# Revit family: mcr FID C
name_source: partatom
category: Akcesoria wentylacyjne
revit_build: Autodesk Revit 2015 (Build: 20160512_1515(x64)
units: mm (PartAtom-declared; Revit-internal decimal feet)

## types (36) — shared parameters
Dokumentacja techniczna = https://mercor.com.pl
Długość = 296 mm  [stored 0.971129 ft]
IfcExportAs = IfcDamperType
IfcExportType = FIREDAMPER
Klasyfikacja obciążenia = Inne
Model = mcr FID S/S c/P
Opis = Niskooporowa przeciwpożarowa klapa jednopłaszczyznowa odcinająca do systemów wentylacji bytowej
Producent = Mercor
URL = http://www.mercor.com.pl

## per-type parameters (varying)
| type | A | E | F | Materiał klapy | Moc pozorna | Napięcie | Nazwa sterowania | Numer | Opis sterowania |
| mcr FID S/S c/P, RST, stal ocynkowana | 50 mm  [stored 0.164042 ft] | 70 mm  [stored 0.229659 ft] | 90 mm  [stored 0.295276 ft] | Mercor - stal ocynkowana, powłoka Zn 275 g/m2 | 0 VA | 0 V | RST | 1 | wyzwalacz termiczny |
| mcr FID S/S c/P, RST/WK1, stal ocynkowana | 50 mm  [stored 0.164042 ft] | 70 mm  [stored 0.229659 ft] | 90 mm  [stored 0.295276 ft] | Mercor - stal ocynkowana, powłoka Zn 275 g/m2 | 0 VA | 0 V | RST/WK1 | 1 | wyzwalacz termiczny + wyłącznik krańcowy (sygnalizacja przegrody zamkniętej) |
| mcr FID S/S c/P, RST/WK2, stal ocynkowana | 50 mm  [stored 0.164042 ft] | 70 mm  [stored 0.229659 ft] | 90 mm  [stored 0.295276 ft] | Mercor - stal ocynkowana, powłoka Zn 275 g/m2 | 0 VA | 0 V | RST/WK2 | 1 | wyzwalacz termiczny + wyłącznik krańcowy (sygnalizacja przegrody zamkniętej/otwartej) |
| mcr FID S/S c/P, RST-KW1/S, stal ocynkowana | 130 mm  [stored 0.426509 ft] | 80 mm  [stored 0.262467 ft] | 100 mm  [stored 0.328084 ft] | Mercor - stal ocynkowana, powłoka Zn 275 g/m2 | 0 VA | 0 V | RST-KW1/S | 2 | wyzwalacz termiczny |
| mcr FID S/S c/P, RST-KW1/S/WK2, stal ocynkowana | 130 mm  [stored 0.426509 ft] | 80 mm  [stored 0.262467 ft] | 100 mm  [stored 0.328084 ft] | Mercor - stal ocynkowana, powłoka Zn 275 g/m2 | 0 VA | 0 V | RST-KW1/S/WK2 | 2 | wyzwalacz termiczny + wyłącznik krańcowy (sygnalizacja przegrody zamkniętej/otwartej) |
| mcr FID S/S c/P, RST-KW1/24I, stal ocynkowana | 130 mm  [stored 0.426509 ft] | 80 mm  [stored 0.262467 ft] | 100 mm  [stored 0.328084 ft] | Mercor - stal ocynkowana, powłoka Zn 275 g/m2 | 4 VA | 24 V | RST-KW1/24I | 2 | wyzwalacz termiczny + wyzwalacz elektromagnetyczny typu impuls, U = 24 V DC + wyłącznik krańcowy (sygnalizacja przegrody zamkniętej/otwartej) |
| mcr FID S/S c/P, RST-KW1/24P, stal ocynkowana | 130 mm  [stored 0.426509 ft] | 80 mm  [stored 0.262467 ft] | 100 mm  [stored 0.328084 ft] | Mercor - stal ocynkowana, powłoka Zn 275 g/m2 | 2 VA | 24 V | RST-KW1/24P | 2 | wyzwalacz termiczny + wyzwalacz elektromagnetyczny typu przerwa, U = 24 V DC + wyłącznik krańcowy (sygnalizacja przegrody zamkniętej/otwartej) |
| mcr FID S/S c/P, RST-KW1/230I, stal ocynkowana | 130 mm  [stored 0.426509 ft] | 80 mm  [stored 0.262467 ft] | 100 mm  [stored 0.328084 ft] | Mercor - stal ocynkowana, powłoka Zn 275 g/m2 | 5 VA | 230 V | RST-KW1/230I | 2 | wyzwalacz termiczny + wyzwalacz elektromagnetyczny typu impuls, U = 230 V AC + wyłącznik krańcowy (sygnalizacja przegrody zamkniętej/otwartej) |
| mcr FID S/S c/P, RST-KW1/230P, stal ocynkowana | 130 mm  [stored 0.426509 ft] | 80 mm  [stored 0.262467 ft] | 100 mm  [stored 0.328084 ft] | Mercor - stal ocynkowana, powłoka Zn 275 g/m2 | 3 VA | 230 V | RST-KW1/230P | 2 | wyzwalacz termiczny + wyzwalacz elektromagnetyczny typu przerwa, U = 230 V AC + wyłącznik krańcowy (sygnalizacja przegrody zamkniętej/otwartej) |
| mcr FID S/S c/P, BF24TL-T-ST, stal ocynkowana | 198 mm  [stored 0.649606 ft] | 65 mm  [stored 0.213255 ft] | 98 mm  [stored 0.321522 ft] | Mercor - stal ocynkowana, powłoka Zn 275 g/m2 | 10 VA | 24 V | BF24TL-T-ST | 3 | siłownik ze sprężyną powrotną, U = 24 V, sterowanie cyfrowe MP Bus (z opcją BKN230-24MP) |
| mcr FID S/S c/P, EXBF24-T, stal ocynkowana | 225 mm  [stored 0.738189 ft] | 175 mm  [stored 0.574147 ft] | 98 mm  [stored 0.321522 ft] | Mercor - stal ocynkowana, powłoka Zn 275 g/m2 | 10 VA | 24 V | EXBF24-T | 4 | przeciwwybuchowy siłownik ze sprężyną powrotną w wersji Ex, U = 24 V AC/DC |
| mcr FID S/S c/P, EXBF230-T, stal ocynkowana | 225 mm  [stored 0.738189 ft] | 175 mm  [stored 0.574147 ft] | 98 mm  [stored 0.321522 ft] | Mercor - stal ocynkowana, powłoka Zn 275 g/m2 | 13 VA | 230 V | EXBF230-T | 4 | przeciwwybuchowy siłownik ze sprężyną powrotną w wersji Ex, U = 230 V AC |
| mcr FID S/S c/P, BFL24-T, stal ocynkowana | 138 mm  [stored 0.452756 ft] | 53 mm  [stored 0.173885 ft] | 98 mm  [stored 0.321522 ft] | Mercor - stal ocynkowana, powłoka Zn 275 g/m2 | 4 VA | 24 V | BFL24-T | 5 | siłownik ze sprężyną powrotną, U = 24 V AC/DC |
| mcr FID S/S c/P, BFL230-T, stal ocynkowana | 138 mm  [stored 0.452756 ft] | 53 mm  [stored 0.173885 ft] | 98 mm  [stored 0.321522 ft] | Mercor - stal ocynkowana, powłoka Zn 275 g/m2 | 7 VA | 230 V | BFL230-T | 5 | siłownik ze sprężyną powrotną, U = 230 V AC |
| mcr FID S/S c/P, BFL24-T-ST, stal ocynkowana | 138 mm  [stored 0.452756 ft] | 53 mm  [stored 0.173885 ft] | 98 mm  [stored 0.321522 ft] | Mercor - stal ocynkowana, powłoka Zn 275 g/m2 | 4 VA | 24 V | BFL24-T-ST | 5 | siłownik ze sprężyną powrotną, do systemu SBS Control (z opcją BKN230-24) |
| mcr FID S/S c/P, BFN24-T, stal ocynkowana | 157 mm  [stored 0.515092 ft] | 57 mm  [stored 0.187008 ft] | 98 mm  [stored 0.321522 ft] | Mercor - stal ocynkowana, powłoka Zn 275 g/m2 | 6 VA | 24 V | BFN24-T | 6 | siłownik ze sprężyną powrotną, U = 24 V AC/DC |
| mcr FID S/S c/P, BFN230-T, stal ocynkowana | 157 mm  [stored 0.515092 ft] | 57 mm  [stored 0.187008 ft] | 98 mm  [stored 0.321522 ft] | Mercor - stal ocynkowana, powłoka Zn 275 g/m2 | 10 VA | 230 V | BFN230-T | 6 | siłownik ze sprężyną powrotną, U = 230 V AC |
| mcr FID S/S c/P, BFN24-T-ST, stal ocynkowana | 157 mm  [stored 0.515092 ft] | 57 mm  [stored 0.187008 ft] | 98 mm  [stored 0.321522 ft] | Mercor - stal ocynkowana, powłoka Zn 275 g/m2 | 6 VA | 24 V | BFN24-T-ST | 6 | siłownik ze sprężyną powrotną, do systemu SBS Control (z opcją BKN230-24) |
| mcr FID S/S c/P, RST, stal nierdzewna | 50 mm  [stored 0.164042 ft] | 70 mm  [stored 0.229659 ft] | 90 mm  [stored 0.295276 ft] | Mercor - stal nierdzewna, kwasoodporna 1.4404 | 0 VA | 0 V | RST | 1 | wyzwalacz termiczny |
| mcr FID S/S c/P, RST/WK1, stal nierdzewna | 50 mm  [stored 0.164042 ft] | 70 mm  [stored 0.229659 ft] | 90 mm  [stored 0.295276 ft] | Mercor - stal nierdzewna, kwasoodporna 1.4404 | 0 VA | 0 V | RST/WK1 | 1 | wyzwalacz termiczny + wyłącznik krańcowy (sygnalizacja przegrody zamkniętej) |
| mcr FID S/S c/P, RST/WK2, stal nierdzewna | 50 mm  [stored 0.164042 ft] | 70 mm  [stored 0.229659 ft] | 90 mm  [stored 0.295276 ft] | Mercor - stal nierdzewna, kwasoodporna 1.4404 | 0 VA | 0 V | RST/WK2 | 1 | wyzwalacz termiczny + wyłącznik krańcowy (sygnalizacja przegrody zamkniętej/otwartej) |
| mcr FID S/S c/P, RST-KW1/S, stal nierdzewna | 130 mm  [stored 0.426509 ft] | 80 mm  [stored 0.262467 ft] | 100 mm  [stored 0.328084 ft] | Mercor - stal nierdzewna, kwasoodporna 1.4404 | 0 VA | 0 V | RST-KW1/S | 2 | wyzwalacz termiczny |
| mcr FID S/S c/P, RST-KW1/S/WK2, stal nierdzewna | 130 mm  [stored 0.426509 ft] | 80 mm  [stored 0.262467 ft] | 100 mm  [stored 0.328084 ft] | Mercor - stal nierdzewna, kwasoodporna 1.4404 | 0 VA | 0 V | RST-KW1/S/WK2 | 2 | wyzwalacz termiczny + wyłącznik krańcowy (sygnalizacja przegrody zamkniętej/otwartej) |
| mcr FID S/S c/P, RST-KW1/24I, stal nierdzewna | 130 mm  [stored 0.426509 ft] | 80 mm  [stored 0.262467 ft] | 100 mm  [stored 0.328084 ft] | Mercor - stal nierdzewna, kwasoodporna 1.4404 | 4 VA | 24 V | RST-KW1/24I | 2 | wyzwalacz termiczny + wyzwalacz elektromagnetyczny typu impuls, U = 24 V DC + wyłącznik krańcowy (sygnalizacja przegrody zamkniętej/otwartej) |
| mcr FID S/S c/P, RST-KW1/24P, stal nierdzewna | 130 mm  [stored 0.426509 ft] | 80 mm  [stored 0.262467 ft] | 100 mm  [stored 0.328084 ft] | Mercor - stal nierdzewna, kwasoodporna 1.4404 | 2 VA | 24 V | RST-KW1/24P | 2 | wyzwalacz termiczny + wyzwalacz elektromagnetyczny typu przerwa, U = 24 V DC + wyłącznik krańcowy (sygnalizacja przegrody zamkniętej/otwartej) |
| mcr FID S/S c/P, RST-KW1/230I, stal nierdzewna | 130 mm  [stored 0.426509 ft] | 80 mm  [stored 0.262467 ft] | 100 mm  [stored 0.328084 ft] | Mercor - stal nierdzewna, kwasoodporna 1.4404 | 5 VA | 230 V | RST-KW1/230I | 2 | wyzwalacz termiczny + wyzwalacz elektromagnetyczny typu impuls, U = 230 V AC + wyłącznik krańcowy (sygnalizacja przegrody zamkniętej/otwartej) |
| mcr FID S/S c/P, RST-KW1/230P, stal nierdzewna | 130 mm  [stored 0.426509 ft] | 80 mm  [stored 0.262467 ft] | 100 mm  [stored 0.328084 ft] | Mercor - stal nierdzewna, kwasoodporna 1.4404 | 3 VA | 230 V | RST-KW1/230P | 2 | wyzwalacz termiczny + wyzwalacz elektromagnetyczny typu przerwa, U = 230 V AC + wyłącznik krańcowy (sygnalizacja przegrody zamkniętej/otwartej) |
| mcr FID S/S c/P, BF24TL-T-ST, stal nierdzewna | 198 mm  [stored 0.649606 ft] | 65 mm  [stored 0.213255 ft] | 98 mm  [stored 0.321522 ft] | Mercor - stal nierdzewna, kwasoodporna 1.4404 | 10 VA | 24 V | BF24TL-T-ST | 3 | siłownik ze sprężyną powrotną, U = 24 V, sterowanie cyfrowe MP Bus (z opcją BKN230-24MP) |
| mcr FID S/S c/P, EXBF24-T, stal nierdzewna | 225 mm  [stored 0.738189 ft] | 175 mm  [stored 0.574147 ft] | 98 mm  [stored 0.321522 ft] | Mercor - stal nierdzewna, kwasoodporna 1.4404 | 10 VA | 24 V | EXBF24-T | 4 | przeciwwybuchowy siłownik ze sprężyną powrotną w wersji Ex, U = 24 V AC/DC |
| mcr FID S/S c/P, EXBF230-T, stal nierdzewna | 225 mm  [stored 0.738189 ft] | 175 mm  [stored 0.574147 ft] | 98 mm  [stored 0.321522 ft] | Mercor - stal nierdzewna, kwasoodporna 1.4404 | 13 VA | 230 V | EXBF230-T | 4 | przeciwwybuchowy siłownik ze sprężyną powrotną w wersji Ex, U = 230 V AC |
| mcr FID S/S c/P, BFL24-T, stal nierdzewna | 138 mm  [stored 0.452756 ft] | 53 mm  [stored 0.173885 ft] | 98 mm  [stored 0.321522 ft] | Mercor - stal nierdzewna, kwasoodporna 1.4404 | 4 VA | 24 V | BFL24-T | 5 | siłownik ze sprężyną powrotną, U = 24 V AC/DC |
| mcr FID S/S c/P, BFL230-T, stal nierdzewna | 138 mm  [stored 0.452756 ft] | 53 mm  [stored 0.173885 ft] | 98 mm  [stored 0.321522 ft] | Mercor - stal nierdzewna, kwasoodporna 1.4404 | 7 VA | 230 V | BFL230-T | 5 | siłownik ze sprężyną powrotną, U = 230 V AC |
| mcr FID S/S c/P, BFL24-T-ST, stal nierdzewna | 138 mm  [stored 0.452756 ft] | 53 mm  [stored 0.173885 ft] | 98 mm  [stored 0.321522 ft] | Mercor - stal nierdzewna, kwasoodporna 1.4404 | 4 VA | 24 V | BFL24-T-ST | 5 | siłownik ze sprężyną powrotną, do systemu SBS Control (z opcją BKN230-24) |
| mcr FID S/S c/P, BFN24-T, stal nierdzewna | 157 mm  [stored 0.515092 ft] | 57 mm  [stored 0.187008 ft] | 98 mm  [stored 0.321522 ft] | Mercor - stal nierdzewna, kwasoodporna 1.4404 | 6 VA | 24 V | BFN24-T | 6 | siłownik ze sprężyną powrotną, U = 24 V AC/DC |
| mcr FID S/S c/P, BFN230-T, stal nierdzewna | 157 mm  [stored 0.515092 ft] | 57 mm  [stored 0.187008 ft] | 98 mm  [stored 0.321522 ft] | Mercor - stal nierdzewna, kwasoodporna 1.4404 | 10 VA | 230 V | BFN230-T | 6 | siłownik ze sprężyną powrotną, U = 230 V AC |
| mcr FID S/S c/P, BFN24-T-ST, stal nierdzewna | 157 mm  [stored 0.515092 ft] | 57 mm  [stored 0.187008 ft] | 98 mm  [stored 0.321522 ft] | Mercor - stal nierdzewna, kwasoodporna 1.4404 | 6 VA | 24 V | BFN24-T-ST | 6 | siłownik ze sprężyną powrotną, do systemu SBS Control (z opcją BKN230-24) |

note: [stored X ft] marks values corroborated as IEEE doubles in the binary element streams (Revit-internal decimal feet)
